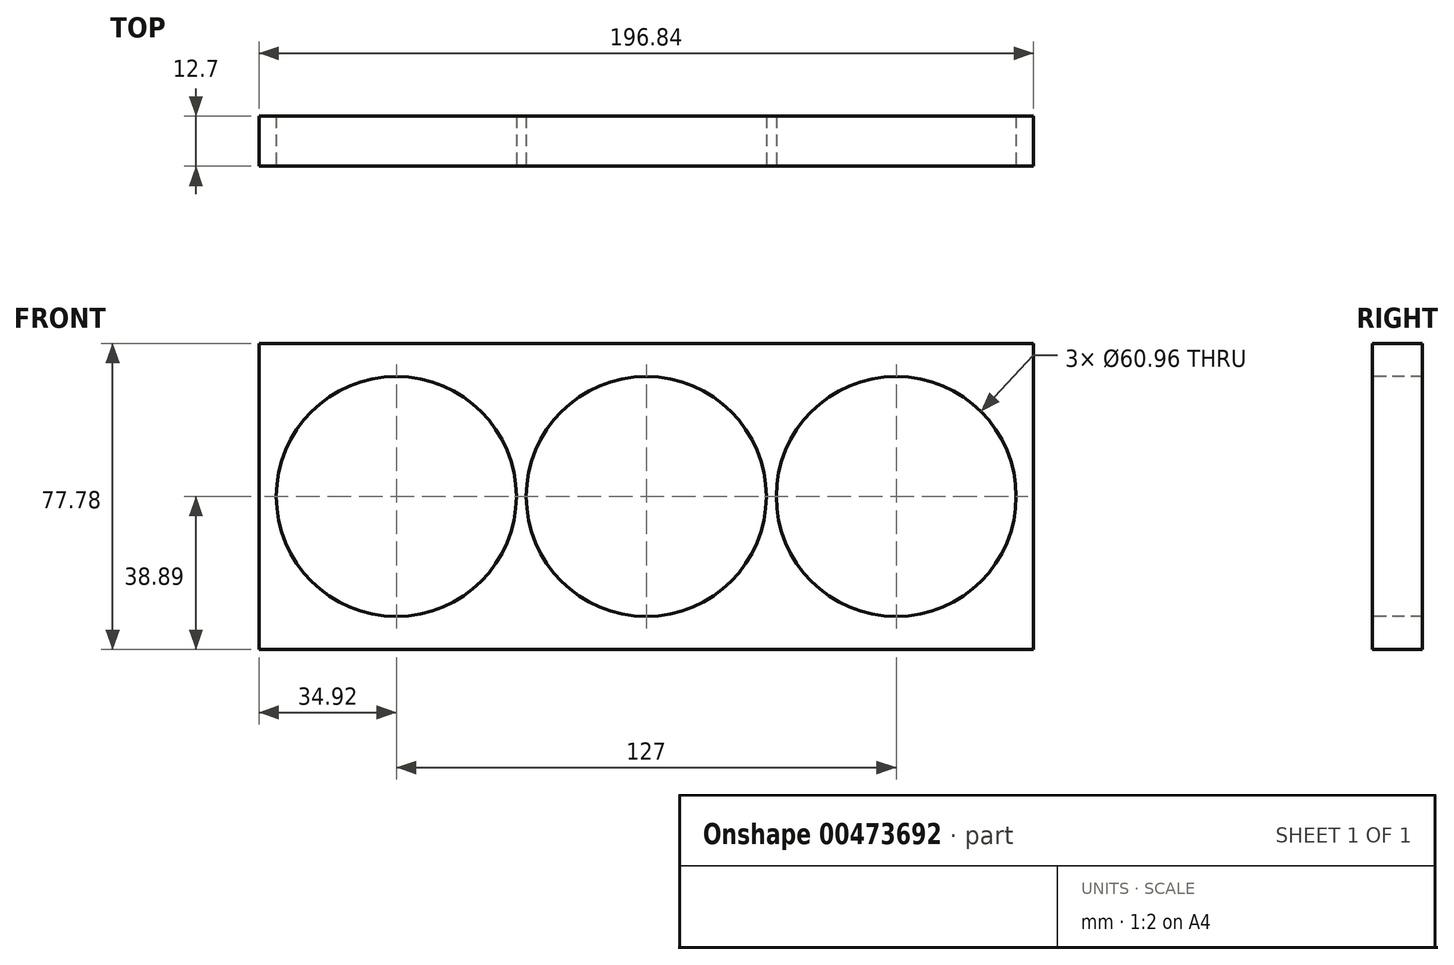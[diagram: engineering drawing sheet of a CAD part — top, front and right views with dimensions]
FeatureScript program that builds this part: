
annotation { "Feature Type Name" : "Feature", "Feature Type Description" : "" }
export const myFeature = defineFeature(function(context is Context, id is Id, definition is map)
    precondition{}
    {
        {
            var Q0;
            Q0=qCreatedBy(makeId("Front.planeOp"),FACE);
            var sketch = newSketch(context, id + "F0", { "sketchPlane" : qUnion([Q0])});
            skCircle(sketch, "E0", {"center": v(0, 0) * mm, "radius": 30.48 * mm});
            skCircle(sketch, "E1.1.0.0", {"center": v(63.5, 0) * mm, "radius": 30.48 * mm});
            skCircle(sketch, "E1.2.0.0", {"center": v(127, 0) * mm, "radius": 30.48 * mm});
            skLineSegment(sketch, "E1.direction1", {"start": v(0, 0) * mm, "end": v(63.5, 0) * mm, "construction": true});
            skLineSegment(sketch, "E2.bottom", {"start": v(161.92, -38.9) * mm, "end": v(-34.92, -38.9) * mm});
            skLineSegment(sketch, "E2.top", {"start": v(161.92, 38.9) * mm, "end": v(-34.92, 38.9) * mm});
            skLineSegment(sketch, "E2.left", {"start": v(161.92, -38.9) * mm, "end": v(161.92, 38.9) * mm});
            skLineSegment(sketch, "E2.right", {"start": v(-34.92, -38.9) * mm, "end": v(-34.92, 38.9) * mm});
            skSolve(sketch);
        }
        {
            var Q0;
            Q0 = qSketchRegion(id + "F0", true);
            extrude(context, id + "F1", {"entities" : qUnion([Q0]), "oppositeDirection" : true, "depth" : 12.7 * mm});
        }
    });
